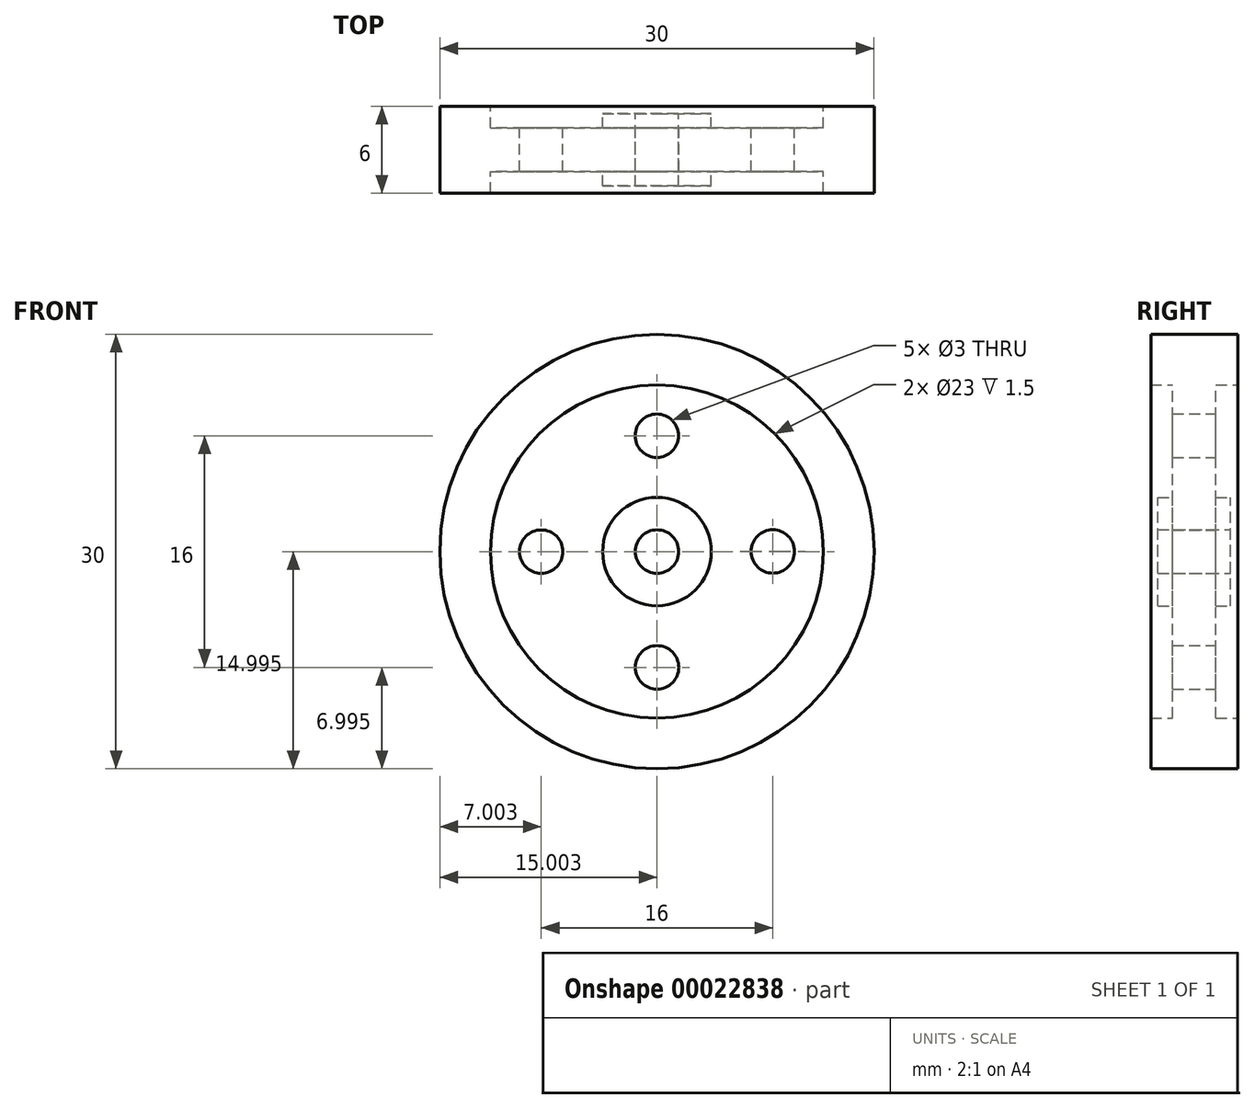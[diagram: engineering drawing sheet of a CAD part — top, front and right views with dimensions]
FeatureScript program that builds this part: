
annotation { "Feature Type Name" : "Feature", "Feature Type Description" : "" }
export const myFeature = defineFeature(function(context is Context, id is Id, definition is map)
    precondition{}
    {
        {
            var Q0;
            Q0=qCreatedBy(makeId("Front.planeOp"),FACE);
            var sketch = newSketch(context, id + "F0", { "sketchPlane" : qUnion([Q0])});
            skCircle(sketch, "E0", {"center": v(-104.43, 49.85) * mm, "radius": 15 * mm});
            skCircle(sketch, "E1", {"center": v(-104.43, 49.85) * mm, "radius": 1.5 * mm});
            skCircle(sketch, "E2", {"center": v(-104.43, 49.85) * mm, "radius": 3.75 * mm});
            skCircle(sketch, "E3", {"center": v(-104.43, 57.85) * mm, "radius": 1.5 * mm});
            skLineSegment(sketch, "E4", {"start": v(-104.43, 57.85) * mm, "end": v(-104.43, 49.85) * mm});
            skCircle(sketch, "E5.1.0", {"center": v(-112.43, 49.84) * mm, "radius": 1.5 * mm});
            skCircle(sketch, "E5.2.0", {"center": v(-104.42, 41.85) * mm, "radius": 1.5 * mm});
            skCircle(sketch, "E6.1.3.0", {"center": v(-96.43, 49.85) * mm, "radius": 1.5 * mm});
            skCircle(sketch, "E7", {"center": v(-104.43, 49.85) * mm, "radius": 11.5 * mm});
            skSolve(sketch);
        }
        {
            var Q0;
            Q0=makeQuery(id+"F0.imprint","IMPRINT",FACE,{"disambiguationData":[TD([[makeQuery(id+"F0.imprint","IMPRINT",EDGE,{"derivedFrom":sQuery(id+"F0.wireOp",EDGE,"E1")}),-1.0]])]});
            extrude(context, id + "F1", {"entities" : qUnion([Q0]), "endBound" : BoundingType.SYMMETRIC, "depth" : 5 * mm});
        }
        {
            var Q0;
            Q0=makeQuery(id+"F0.imprint","IMPRINT",FACE,{"disambiguationData":[TD([[makeQuery(id+"F0.imprint","IMPRINT",EDGE,{"derivedFrom":sQuery(id+"F0.wireOp",EDGE,"E2")}),-1.0]])]});
            extrude(context, id + "F2", {"entities" : qUnion([Q0]), "operationType" : NewBodyOperationType.ADD, "endBound" : BoundingType.SYMMETRIC, "depth" : 3 * mm});
        }
        {
            var Q0;
            Q0=makeQuery(id+"F0.imprint","IMPRINT",FACE,{"disambiguationData":[TD([[makeQuery(id+"F0.imprint","IMPRINT",EDGE,{"derivedFrom":sQuery(id+"F0.wireOp",EDGE,"E0")}),1.0]])]});
            extrude(context, id + "F3", {"entities" : qUnion([Q0]), "operationType" : NewBodyOperationType.ADD, "endBound" : BoundingType.SYMMETRIC, "depth" : 6 * mm});
        }
    });
